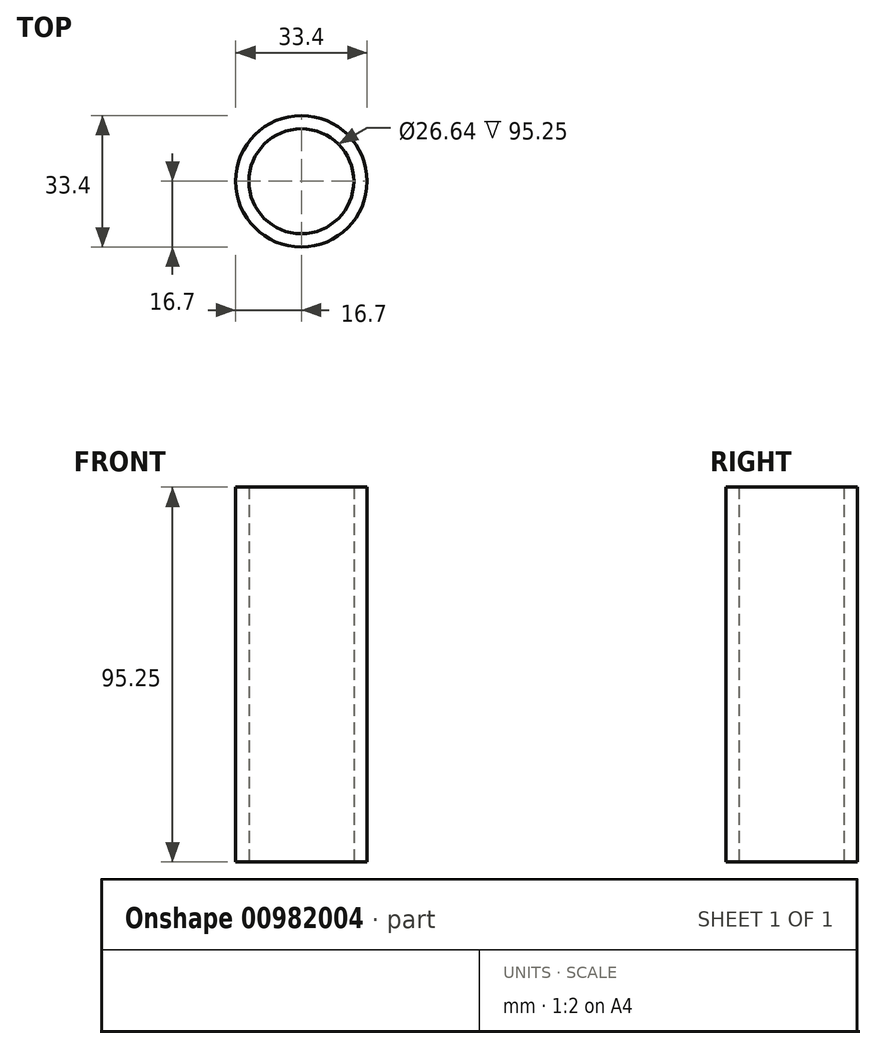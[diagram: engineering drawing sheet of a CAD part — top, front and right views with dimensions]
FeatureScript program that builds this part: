
annotation { "Feature Type Name" : "Feature", "Feature Type Description" : "" }
export const myFeature = defineFeature(function(context is Context, id is Id, definition is map)
    precondition{}
    {
        {
            var Q0;
            Q0=qCreatedBy(makeId("Top.planeOp"),FACE);
            var sketch = newSketch(context, id + "F0", { "sketchPlane" : qUnion([Q0])});
            skCircle(sketch, "E0", {"center": v(0, 0) * mm, "radius": 13.32 * mm});
            skCircle(sketch, "E1", {"center": v(0, 0) * mm, "radius": 16.7 * mm});
            skSolve(sketch);
        }
        {
            var Q0;
            Q0=qSketchRegion(id+"F0",true);
            extrude(context, id + "F1", {"entities" : qUnion([Q0]), "depth" : 95.25 * mm, "offsetDistance" : 25.4 * mm});
        }
    });
